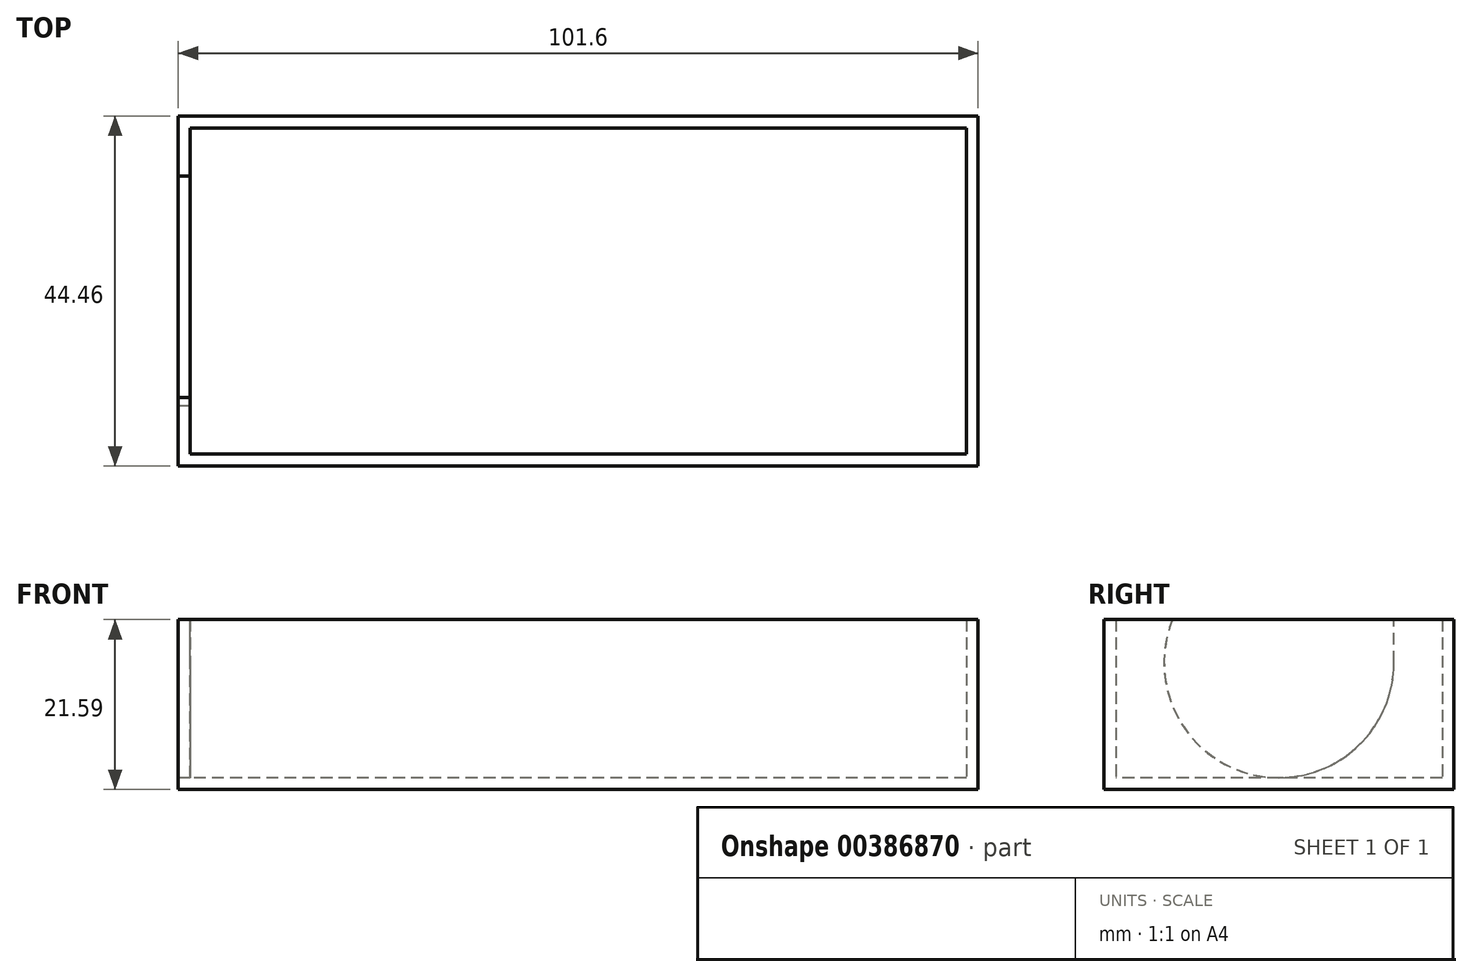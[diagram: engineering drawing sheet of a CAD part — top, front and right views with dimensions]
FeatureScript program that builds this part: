
annotation { "Feature Type Name" : "Feature", "Feature Type Description" : "" }
export const myFeature = defineFeature(function(context is Context, id is Id, definition is map)
    precondition{}
    {
        {
            var Q0;
            Q0=qCreatedBy(makeId("Top.planeOp"),FACE);
            var sketch = newSketch(context, id + "F0", { "sketchPlane" : qUnion([Q0])});
            skLineSegment(sketch, "E0.bottom", {"start": v(50.8, 22.23) * mm, "end": v(-50.8, 22.23) * mm});
            skLineSegment(sketch, "E0.top", {"start": v(50.8, -22.23) * mm, "end": v(-50.8, -22.23) * mm});
            skLineSegment(sketch, "E0.left", {"start": v(50.8, 22.23) * mm, "end": v(50.8, -22.23) * mm});
            skLineSegment(sketch, "E0.right", {"start": v(-50.8, 22.23) * mm, "end": v(-50.8, -22.23) * mm});
            skPoint(sketch, "E0.middle", {"position": v(0, 0) * mm});
            skSolve(sketch);
        }
        {
            var Q0;
            Q0=makeQuery(id+"F0.imprint","IMPRINT",FACE,{"disambiguationData":[TD([[makeQuery(id+"F0.imprint","IMPRINT",EDGE,{"derivedFrom":sQuery(id+"F0.wireOp",EDGE,"E0.bottom")}),1.0]])]});
            extrude(context, id + "F1", {"entities" : qUnion([Q0]), "depth" : 21.59 * mm, "offsetDistance" : 25.4 * mm});
        }
        {
            var Q0;
            Q0=makeQuery(id+"F1.opExtrude","CAP_FACE",FACE,{"disambiguationData":[OSD([sQuery(id+"F0.wireOp",EDGE,"E0.bottom"),sQuery(id+"F0.wireOp",EDGE,"E0.top"),sQuery(id+"F0.wireOp",EDGE,"E0.left"),sQuery(id+"F0.wireOp",EDGE,"E0.right")])],"isStart":false});
            shell(context, id + "F2", {"entities" : qUnion([Q0]), "thickness" : 1.5 * mm});
        }
        {
            var Q0;
            Q0=makeQuery(id+"F1.opExtrude","SWEPT_FACE",FACE,{"disambiguationData":[OSD([sQuery(id+"F0.wireOp",EDGE,"E0.right")])]});
            var sketch = newSketch(context, id + "F3", { "sketchPlane" : qUnion([Q0])});
            skCircle(sketch, "E1", {"center": v(0, 16.1) * mm, "radius": 14.6 * mm});
            skLineSegment(sketch, "E2", {"start": v(-14.6, 15.47) * mm, "end": v(-14.6, 21.59) * mm});
            skLineSegment(sketch, "E3", {"start": v(14.6, 16.56) * mm, "end": v(14.6, 21.59) * mm});
            skLineSegment(sketch, "E4", {"start": v(14.6, 21.59) * mm, "end": v(14.49, 21.9) * mm});
            skSolve(sketch);
        }
        {
            var Q0;
            {var subQ0=sQuery(id+"F3.wireOp",EDGE,"E2");var subQ1=sQuery(id+"F3.wireOp",EDGE,"E1");var subQ2=makeQuery(id+"F3.imprint","INTERSECT",VERTEX,{"disambiguationData":[OD(1.0)],"derivedFrom":[subQ1,subQ0]});Q0=makeQuery(id+"F3.imprint","IMPRINT",FACE,{"disambiguationData":[TD([[makeQuery(id+"F3.imprint","IMPRINT",EDGE,{"disambiguationData":[TD([[subQ2,1.0]])],"derivedFrom":subQ1}),-1.0]])]});}
            var Q1;
            {var subQ1=sQuery(id+"F3.wireOp",EDGE,"E1");var subQ3=makeQuery(id+"F3.imprint","INTERSECT",VERTEX,{"derivedFrom":[subQ1,sQuery(id+"F3.wireOp",EDGE,"E3")]});Q1=makeQuery(id+"F3.imprint","IMPRINT",FACE,{"disambiguationData":[TD([[makeQuery(id+"F3.imprint","IMPRINT",EDGE,{"disambiguationData":[TD([[subQ3,-1.0]])],"derivedFrom":subQ1}),1.0]])]});}
            var Q2;
            {var subQ0=sQuery(id+"F3.wireOp",EDGE,"E3");Q2=makeQuery(id+"F3.imprint","IMPRINT",FACE,{"disambiguationData":[TD([[makeQuery(id+"F3.imprint","IMPRINT",EDGE,{"derivedFrom":subQ0}),1.0]])]});}
            extrude(context, id + "F4", {"entities" : qUnion([Q0, Q1, Q2]), "operationType" : NewBodyOperationType.REMOVE, "oppositeDirection" : true, "depth" : 1.5 * mm});
        }
    });
